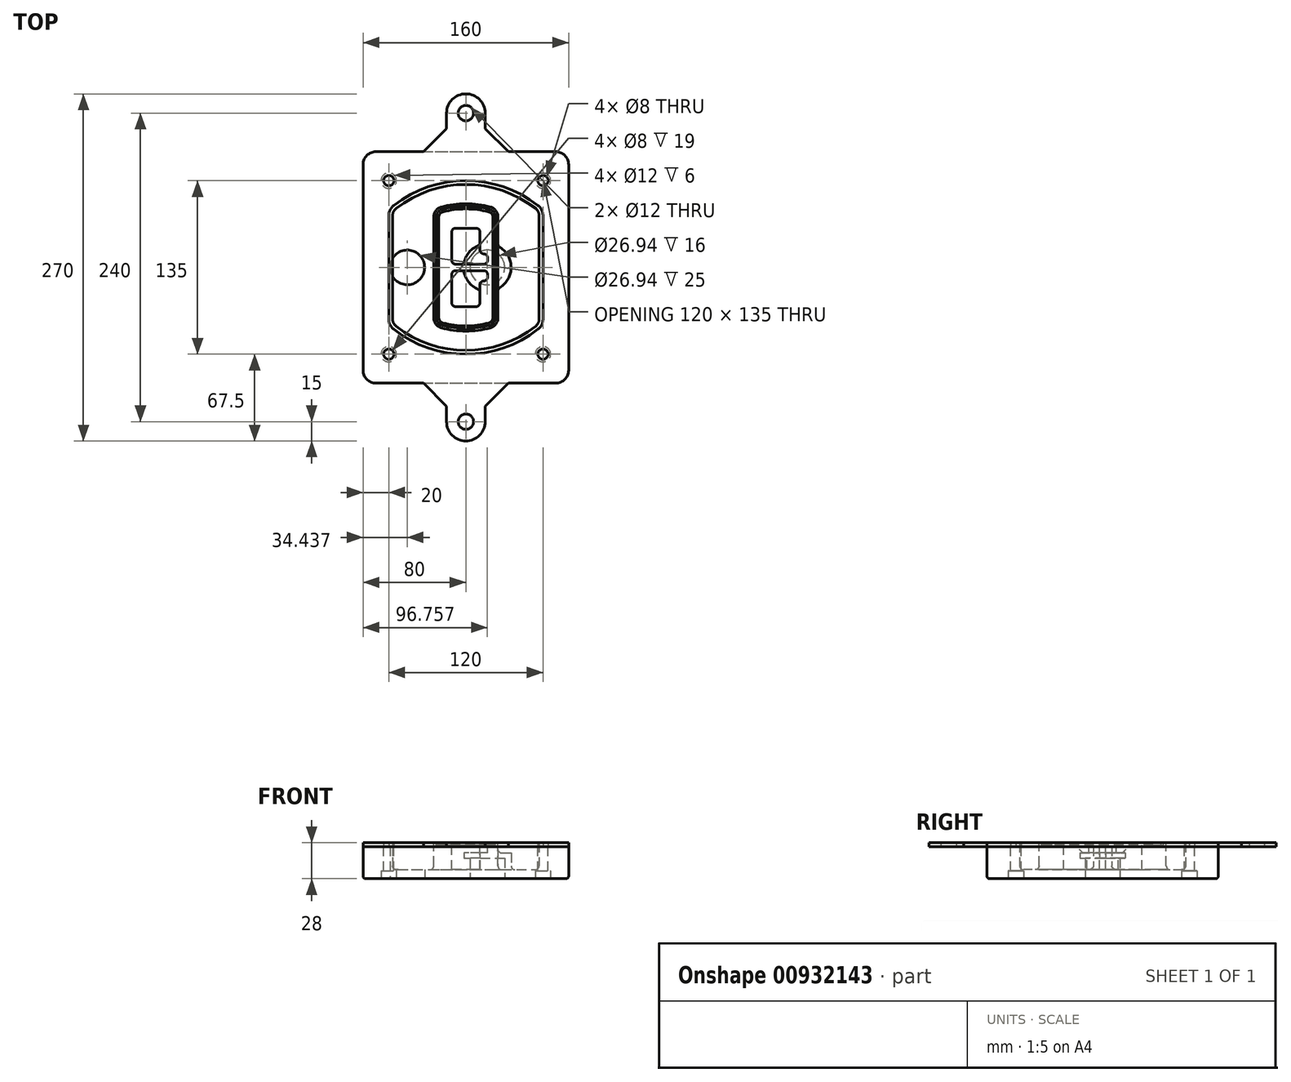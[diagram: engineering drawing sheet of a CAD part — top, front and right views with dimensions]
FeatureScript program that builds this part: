
annotation { "Feature Type Name" : "Feature", "Feature Type Description" : "" }
export const myFeature = defineFeature(function(context is Context, id is Id, definition is map)
    precondition{}
    {
        {
            var Q0;
            Q0=qCreatedBy(makeId("Top.planeOp"),FACE);
            var sketch = newSketch(context, id + "F0", { "sketchPlane" : qUnion([Q0])});
            skPoint(sketch, "E0.rect.middle", {"position": v(0, 0) * mm});
            skLineSegment(sketch, "E1.bottom", {"start": v(-70, -90) * mm, "end": v(70, -90) * mm});
            skLineSegment(sketch, "E1.top", {"start": v(-70, 90) * mm, "end": v(70, 90) * mm});
            skLineSegment(sketch, "E1.left", {"start": v(-80, -80) * mm, "end": v(-80, 80) * mm});
            skLineSegment(sketch, "E1.right", {"start": v(80, -80) * mm, "end": v(80, 80) * mm});
            skLineSegment(sketch, "E2", {"start": v(-80, 90) * mm, "end": v(80, -90) * mm, "construction": true});
            skLineSegment(sketch, "E3", {"start": v(80, 90) * mm, "end": v(-80, -90) * mm, "construction": true});
            skCircle(sketch, "E4", {"center": v(-60, 67.5) * mm, "radius": 4 * mm});
            skCircle(sketch, "E5", {"center": v(60, 67.5) * mm, "radius": 4 * mm});
            skCircle(sketch, "E6", {"center": v(60, -67.5) * mm, "radius": 4 * mm});
            skCircle(sketch, "E7", {"center": v(-60, -67.5) * mm, "radius": 4 * mm});
            skLineSegment(sketch, "E8", {"start": v(-60, 67.5) * mm, "end": v(60, 67.5) * mm, "construction": true});
            skLineSegment(sketch, "E9", {"start": v(60, 67.5) * mm, "end": v(60, -67.5) * mm, "construction": true});
            skLineSegment(sketch, "E10", {"start": v(60, -67.5) * mm, "end": v(-60, -67.5) * mm, "construction": true});
            skLineSegment(sketch, "E11", {"start": v(-60, -67.5) * mm, "end": v(-60, 67.5) * mm, "construction": true});
            skLineSegment(sketch, "E12", {"start": v(-60, 40.3) * mm, "end": v(-60, -40.3) * mm});
            skLineSegment(sketch, "E13", {"start": v(60, 40.3) * mm, "end": v(60, -40.3) * mm});
            skArc(sketch, "E14", {"start": v(56.15, 48.18) * mm, "mid": v(0, 67.5) * mm, "end": v(-56.15, 48.18) * mm});
            skArc(sketch, "E15", {"start": v(-56.15, -48.18) * mm, "mid": v(0, -67.5) * mm, "end": v(56.15, -48.18) * mm});
            skLineSegment(sketch, "E16", {"start": v(-60, 0) * mm, "end": v(60, 0) * mm, "construction": true});
            skPoint(sketch, "E17.visualSharp", {"position": v(-60, -45) * mm});
            skArc(sketch, "E17.filletArc", {"start": v(-60, -40.3) * mm, "mid": v(-58.99, -44.68) * mm, "end": v(-56.15, -48.18) * mm});
            skPoint(sketch, "E18.visualSharp", {"position": v(-60, 45) * mm});
            skArc(sketch, "E18.filletArc", {"start": v(-56.15, 48.18) * mm, "mid": v(-58.99, 44.68) * mm, "end": v(-60, 40.3) * mm});
            skPoint(sketch, "E19.visualSharp", {"position": v(60, 45) * mm});
            skArc(sketch, "E19.filletArc", {"start": v(60, 40.3) * mm, "mid": v(58.99, 44.68) * mm, "end": v(56.15, 48.18) * mm});
            skPoint(sketch, "E20.visualSharp", {"position": v(60, -45) * mm});
            skArc(sketch, "E20.filletArc", {"start": v(56.15, -48.18) * mm, "mid": v(58.99, -44.68) * mm, "end": v(60, -40.3) * mm});
            skPoint(sketch, "E21.visualSharp", {"position": v(-80, 90) * mm});
            skArc(sketch, "E21.filletArc", {"start": v(-70, 90) * mm, "mid": v(-77.07, 87.07) * mm, "end": v(-80, 80) * mm});
            skPoint(sketch, "E22.visualSharp", {"position": v(80, 90) * mm});
            skArc(sketch, "E22.filletArc", {"start": v(80, 80) * mm, "mid": v(77.07, 87.07) * mm, "end": v(70, 90) * mm});
            skPoint(sketch, "E23.visualSharp", {"position": v(80, -90) * mm});
            skArc(sketch, "E23.filletArc", {"start": v(70, -90) * mm, "mid": v(77.07, -87.07) * mm, "end": v(80, -80) * mm});
            skPoint(sketch, "E24.visualSharp", {"position": v(-80, -90) * mm});
            skArc(sketch, "E24.filletArc", {"start": v(-80, -80) * mm, "mid": v(-77.07, -87.07) * mm, "end": v(-70, -90) * mm});
            skArc(sketch, "E25.0", {"start": v(57, 40.3) * mm, "mid": v(56.3, 43.36) * mm, "end": v(54.3, 45.81) * mm});
            skLineSegment(sketch, "E25.1", {"start": v(57, 40.3) * mm, "end": v(57, -40.3) * mm});
            skArc(sketch, "E25.2", {"start": v(54.3, -45.81) * mm, "mid": v(56.3, -43.36) * mm, "end": v(57, -40.3) * mm});
            skArc(sketch, "E25.3", {"start": v(-54.3, -45.81) * mm, "mid": v(0, -64.5) * mm, "end": v(54.3, -45.81) * mm});
            skArc(sketch, "E25.4", {"start": v(-57, -40.3) * mm, "mid": v(-56.3, -43.36) * mm, "end": v(-54.3, -45.81) * mm});
            skArc(sketch, "E25.5", {"start": v(54.3, 45.81) * mm, "mid": v(0, 64.5) * mm, "end": v(-54.3, 45.81) * mm});
            skLineSegment(sketch, "E25.6", {"start": v(-57, 40.3) * mm, "end": v(-57, -40.3) * mm});
            skArc(sketch, "E25.7", {"start": v(-54.3, 45.81) * mm, "mid": v(-56.3, 43.36) * mm, "end": v(-57, 40.3) * mm});
            skArc(sketch, "E26.0", {"start": v(-58.62, 51.33) * mm, "mid": v(-62.58, 46.43) * mm, "end": v(-64, 40.3) * mm});
            skArc(sketch, "E26.1", {"start": v(58.62, 51.33) * mm, "mid": v(0, 71.5) * mm, "end": v(-58.62, 51.33) * mm});
            skArc(sketch, "E26.2", {"start": v(64, 40.3) * mm, "mid": v(62.58, 46.43) * mm, "end": v(58.62, 51.33) * mm});
            skLineSegment(sketch, "E26.3", {"start": v(64, 40.3) * mm, "end": v(64, -40.3) * mm});
            skArc(sketch, "E26.4", {"start": v(58.62, -51.33) * mm, "mid": v(62.58, -46.43) * mm, "end": v(64, -40.3) * mm});
            skLineSegment(sketch, "E26.5", {"start": v(-64, 40.3) * mm, "end": v(-64, -40.3) * mm});
            skArc(sketch, "E26.6", {"start": v(-58.62, -51.33) * mm, "mid": v(0, -71.5) * mm, "end": v(58.62, -51.33) * mm});
            skArc(sketch, "E26.7", {"start": v(-64, -40.3) * mm, "mid": v(-62.58, -46.43) * mm, "end": v(-58.62, -51.33) * mm});
            skSolve(sketch);
        }
        {
            var Q0;
            Q0=makeQuery(id+"F0.imprint","IMPRINT",FACE,{"disambiguationData":[TD([[makeQuery(id+"F0.imprint","IMPRINT",EDGE,{"derivedFrom":sQuery(id+"F0.wireOp",EDGE,"E1.bottom")}),1.0]])]});
            var Q1;
            Q1=makeQuery(id+"F0.imprint","IMPRINT",FACE,{"disambiguationData":[TD([[makeQuery(id+"F0.imprint","IMPRINT",EDGE,{"derivedFrom":sQuery(id+"F0.wireOp",EDGE,"E12")}),1.0]])]});
            var Q2;
            Q2=makeQuery(id+"F0.imprint","IMPRINT",FACE,{"disambiguationData":[TD([[makeQuery(id+"F0.imprint","IMPRINT",EDGE,{"derivedFrom":sQuery(id+"F0.wireOp",EDGE,"E25.0")}),1.0]])]});
            var Q3;
            Q3=makeQuery(id+"F0.imprint","IMPRINT",FACE,{"disambiguationData":[TD([[makeQuery(id+"F0.imprint","IMPRINT",EDGE,{"derivedFrom":sQuery(id+"F0.wireOp",EDGE,"E12")}),-1.0]])]});
            extrude(context, id + "F1", {"entities" : qUnion([Q0, Q1, Q2, Q3]), "oppositeDirection" : true, "depth" : 25 * mm});
        }
        {
            var Q0;
            Q0=makeQuery(id+"F0.imprint","IMPRINT",FACE,{"disambiguationData":[TD([[makeQuery(id+"F0.imprint","IMPRINT",EDGE,{"derivedFrom":sQuery(id+"F0.wireOp",EDGE,"E12")}),1.0]])]});
            extrude(context, id + "F2", {"entities" : qUnion([Q0]), "operationType" : NewBodyOperationType.ADD, "depth" : 3 * mm});
        }
        {
            var Q0;
            Q0=makeQuery(id+"F0.imprint","IMPRINT",FACE,{"disambiguationData":[TD([[makeQuery(id+"F0.imprint","IMPRINT",EDGE,{"derivedFrom":sQuery(id+"F0.wireOp",EDGE,"E25.0")}),1.0]])]});
            extrude(context, id + "F3", {"entities" : qUnion([Q0]), "operationType" : NewBodyOperationType.REMOVE, "oppositeDirection" : true, "depth" : 18 * mm});
        }
        {
            var Q0;
            Q0=makeQuery(id+"F2.opExtrude","CAP_FACE",FACE,{"disambiguationData":[OSD([sQuery(id+"F0.wireOp",EDGE,"E12"),sQuery(id+"F0.wireOp",EDGE,"E13"),sQuery(id+"F0.wireOp",EDGE,"E14"),sQuery(id+"F0.wireOp",EDGE,"E15"),sQuery(id+"F0.wireOp",EDGE,"E17.filletArc"),sQuery(id+"F0.wireOp",EDGE,"E18.filletArc"),sQuery(id+"F0.wireOp",EDGE,"E19.filletArc"),sQuery(id+"F0.wireOp",EDGE,"E20.filletArc"),sQuery(id+"F0.wireOp",EDGE,"E25.0"),sQuery(id+"F0.wireOp",EDGE,"E25.1"),sQuery(id+"F0.wireOp",EDGE,"E25.2"),sQuery(id+"F0.wireOp",EDGE,"E25.3"),sQuery(id+"F0.wireOp",EDGE,"E25.4"),sQuery(id+"F0.wireOp",EDGE,"E25.5"),sQuery(id+"F0.wireOp",EDGE,"E25.6"),sQuery(id+"F0.wireOp",EDGE,"E25.7")])],"isStart":false});
            var sketch = newSketch(context, id + "F4", { "sketchPlane" : qUnion([Q0])});
            skArc(sketch, "E27.0", {"start": v(-19.08, -46.97) * mm, "mid": v(0, -49.5) * mm, "end": v(19.08, -46.97) * mm});
            skArc(sketch, "E28.0", {"start": v(19.08, 46.97) * mm, "mid": v(0, 49.5) * mm, "end": v(-19.08, 46.97) * mm});
            skLineSegment(sketch, "E29", {"start": v(-25, 39.25) * mm, "end": v(-25, -39.25) * mm});
            skLineSegment(sketch, "E30", {"start": v(25, 39.25) * mm, "end": v(25, -39.25) * mm});
            skLineSegment(sketch, "E31", {"start": v(-25, 45.1) * mm, "end": v(25, 45.1) * mm, "construction": true});
            skLineSegment(sketch, "E32", {"start": v(-25, -45.1) * mm, "end": v(25, -45.1) * mm, "construction": true});
            skPoint(sketch, "E33.visualSharp", {"position": v(-25, 45.1) * mm});
            skArc(sketch, "E33.filletArc", {"start": v(-19.08, 46.97) * mm, "mid": v(-23.35, 44.11) * mm, "end": v(-25, 39.25) * mm});
            skPoint(sketch, "E34.visualSharp", {"position": v(25, 45.1) * mm});
            skArc(sketch, "E34.filletArc", {"start": v(25, 39.25) * mm, "mid": v(23.35, 44.11) * mm, "end": v(19.08, 46.97) * mm});
            skPoint(sketch, "E35.visualSharp", {"position": v(25, -45.1) * mm});
            skArc(sketch, "E35.filletArc", {"start": v(19.08, -46.97) * mm, "mid": v(23.35, -44.11) * mm, "end": v(25, -39.25) * mm});
            skPoint(sketch, "E36.visualSharp", {"position": v(-25, -45.1) * mm});
            skArc(sketch, "E36.filletArc", {"start": v(-25, -39.25) * mm, "mid": v(-23.35, -44.11) * mm, "end": v(-19.08, -46.97) * mm});
            skArc(sketch, "E37.0", {"start": v(54.3, 45.81) * mm, "mid": v(0, 64.5) * mm, "end": v(-54.3, 45.81) * mm});
            skArc(sketch, "E37.1", {"start": v(-54.3, 45.81) * mm, "mid": v(-56.3, 43.36) * mm, "end": v(-57, 40.3) * mm});
            skLineSegment(sketch, "E37.2", {"start": v(-57, 40.3) * mm, "end": v(-57, -40.3) * mm});
            skArc(sketch, "E37.3", {"start": v(-57, -40.3) * mm, "mid": v(-56.3, -43.36) * mm, "end": v(-54.3, -45.81) * mm});
            skArc(sketch, "E37.4", {"start": v(-54.3, -45.81) * mm, "mid": v(0, -64.5) * mm, "end": v(54.3, -45.81) * mm});
            skArc(sketch, "E37.5", {"start": v(54.3, -45.81) * mm, "mid": v(56.3, -43.36) * mm, "end": v(57, -40.3) * mm});
            skLineSegment(sketch, "E37.6", {"start": v(57, 40.3) * mm, "end": v(57, -40.3) * mm});
            skArc(sketch, "E37.7", {"start": v(57, 40.3) * mm, "mid": v(56.3, 43.36) * mm, "end": v(54.3, 45.81) * mm});
            skLineSegment(sketch, "E38.0", {"start": v(23, 39.25) * mm, "end": v(23, -39.25) * mm});
            skArc(sketch, "E38.1", {"start": v(18.56, -45.04) * mm, "mid": v(21.76, -42.9) * mm, "end": v(23, -39.25) * mm});
            skArc(sketch, "E38.2", {"start": v(-18.56, -45.04) * mm, "mid": v(0, -47.5) * mm, "end": v(18.56, -45.04) * mm});
            skArc(sketch, "E38.3", {"start": v(-23, -39.25) * mm, "mid": v(-21.76, -42.9) * mm, "end": v(-18.56, -45.04) * mm});
            skLineSegment(sketch, "E38.4", {"start": v(-23, 39.25) * mm, "end": v(-23, -39.25) * mm});
            skArc(sketch, "E38.5", {"start": v(23, 39.25) * mm, "mid": v(21.76, 42.9) * mm, "end": v(18.56, 45.04) * mm});
            skArc(sketch, "E38.6", {"start": v(-18.56, 45.04) * mm, "mid": v(-21.76, 42.9) * mm, "end": v(-23, 39.25) * mm});
            skArc(sketch, "E38.7", {"start": v(18.56, 45.04) * mm, "mid": v(0, 47.5) * mm, "end": v(-18.56, 45.04) * mm});
            skArc(sketch, "E39.0", {"start": v(21, 39.25) * mm, "mid": v(20.18, 41.68) * mm, "end": v(18.04, 43.1) * mm});
            skLineSegment(sketch, "E39.1", {"start": v(21, 39.25) * mm, "end": v(21, -39.25) * mm});
            skArc(sketch, "E39.2", {"start": v(18.04, -43.1) * mm, "mid": v(20.18, -41.68) * mm, "end": v(21, -39.25) * mm});
            skArc(sketch, "E39.3", {"start": v(-18.04, -43.1) * mm, "mid": v(0, -45.5) * mm, "end": v(18.04, -43.1) * mm});
            skArc(sketch, "E39.4", {"start": v(-21, -39.25) * mm, "mid": v(-20.18, -41.68) * mm, "end": v(-18.04, -43.1) * mm});
            skArc(sketch, "E39.5", {"start": v(18.04, 43.1) * mm, "mid": v(0, 45.5) * mm, "end": v(-18.04, 43.1) * mm});
            skLineSegment(sketch, "E39.6", {"start": v(-21, 39.25) * mm, "end": v(-21, -39.25) * mm});
            skArc(sketch, "E39.7", {"start": v(-18.04, 43.1) * mm, "mid": v(-20.18, 41.68) * mm, "end": v(-21, 39.25) * mm});
            skLineSegment(sketch, "E40", {"start": v(-25, 0) * mm, "end": v(25, 0) * mm, "construction": true});
            skLineSegment(sketch, "E41", {"start": v(-11, 5.5) * mm, "end": v(-11, 27.5) * mm});
            skLineSegment(sketch, "E42", {"start": v(-8, 30.5) * mm, "end": v(8, 30.5) * mm});
            skLineSegment(sketch, "E43", {"start": v(11, 27.5) * mm, "end": v(11, 13.5) * mm});
            skLineSegment(sketch, "E44", {"start": v(14, 10.5) * mm, "end": v(14, 10.5) * mm});
            skLineSegment(sketch, "E45", {"start": v(17, 7.5) * mm, "end": v(17, 5.5) * mm});
            skLineSegment(sketch, "E46", {"start": v(14, 2.5) * mm, "end": v(-8, 2.5) * mm});
            skPoint(sketch, "E47.visualSharp", {"position": v(-11, 30.5) * mm});
            skArc(sketch, "E47.filletArc", {"start": v(-8, 30.5) * mm, "mid": v(-10.12, 29.62) * mm, "end": v(-11, 27.5) * mm});
            skPoint(sketch, "E48.visualSharp", {"position": v(11, 30.5) * mm});
            skArc(sketch, "E48.filletArc", {"start": v(11, 27.5) * mm, "mid": v(10.12, 29.62) * mm, "end": v(8, 30.5) * mm});
            skPoint(sketch, "E49.visualSharp", {"position": v(11, 10.5) * mm});
            skArc(sketch, "E49.filletArc", {"start": v(11, 13.5) * mm, "mid": v(11.88, 11.38) * mm, "end": v(14, 10.5) * mm});
            skPoint(sketch, "E50.visualSharp", {"position": v(17, 10.5) * mm});
            skArc(sketch, "E50.filletArc", {"start": v(17, 7.5) * mm, "mid": v(16.12, 9.62) * mm, "end": v(14, 10.5) * mm});
            skPoint(sketch, "E51.visualSharp", {"position": v(17, 2.5) * mm});
            skArc(sketch, "E51.filletArc", {"start": v(14, 2.5) * mm, "mid": v(16.12, 3.38) * mm, "end": v(17, 5.5) * mm});
            skPoint(sketch, "E52.visualSharp", {"position": v(-11, 2.5) * mm});
            skArc(sketch, "E52.filletArc", {"start": v(-11, 5.5) * mm, "mid": v(-10.12, 3.38) * mm, "end": v(-8, 2.5) * mm});
            skLineSegment(sketch, "E53.0.MirrorCS", {"start": v(14, -2.5) * mm, "end": v(-8, -2.5) * mm});
            skArc(sketch, "E54.0.MirrorCS", {"start": v(-11, -5.5) * mm, "mid": v(-10.12, -3.38) * mm, "end": v(-8, -2.5) * mm});
            skLineSegment(sketch, "E55.0.MirrorCS", {"start": v(-11, -5.5) * mm, "end": v(-11, -27.5) * mm});
            skArc(sketch, "E56.0.MirrorCS", {"start": v(-8, -30.5) * mm, "mid": v(-10.12, -29.62) * mm, "end": v(-11, -27.5) * mm});
            skLineSegment(sketch, "E57.0.MirrorCS", {"start": v(-8, -30.5) * mm, "end": v(8, -30.5) * mm});
            skArc(sketch, "E58.0.MirrorCS", {"start": v(11, -27.5) * mm, "mid": v(10.12, -29.62) * mm, "end": v(8, -30.5) * mm});
            skLineSegment(sketch, "E59.0.MirrorCS", {"start": v(11, -27.5) * mm, "end": v(11, -13.5) * mm});
            skArc(sketch, "E60.0.MirrorCS", {"start": v(11, -13.5) * mm, "mid": v(11.88, -11.38) * mm, "end": v(14, -10.5) * mm});
            skArc(sketch, "E61.0.MirrorCS", {"start": v(17, -7.5) * mm, "mid": v(16.12, -9.62) * mm, "end": v(14, -10.5) * mm});
            skLineSegment(sketch, "E62.0.MirrorCS", {"start": v(17, -7.5) * mm, "end": v(17, -5.5) * mm});
            skArc(sketch, "E63.0.MirrorCS", {"start": v(14, -2.5) * mm, "mid": v(16.12, -3.38) * mm, "end": v(17, -5.5) * mm});
            skSolve(sketch);
        }
        {
            var Q0;
            Q0=makeQuery(id+"F4.imprint","IMPRINT",FACE,{"disambiguationData":[TD([[makeQuery(id+"F4.imprint","IMPRINT",EDGE,{"derivedFrom":sQuery(id+"F4.wireOp",EDGE,"E27.0")}),1.0]])]});
            var Q1;
            Q1=makeQuery(id+"F4.imprint","IMPRINT",FACE,{"disambiguationData":[TD([[makeQuery(id+"F4.imprint","IMPRINT",EDGE,{"derivedFrom":sQuery(id+"F4.wireOp",EDGE,"E38.0")}),-1.0]])]});
            var Q2;
            Q2=makeQuery(id+"F4.imprint","IMPRINT",FACE,{"disambiguationData":[TD([[makeQuery(id+"F4.imprint","IMPRINT",EDGE,{"derivedFrom":sQuery(id+"F4.wireOp",EDGE,"E39.0")}),1.0]])]});
            extrude(context, id + "F5", {"entities" : qUnion([Q0, Q1, Q2]), "operationType" : NewBodyOperationType.ADD, "endBound" : BoundingType.UP_TO_NEXT, "oppositeDirection" : true, "depth" : 25 * mm});
        }
        {
            var Q0;
            Q0=makeQuery(id+"F4.imprint","IMPRINT",FACE,{"disambiguationData":[TD([[makeQuery(id+"F4.imprint","IMPRINT",EDGE,{"derivedFrom":sQuery(id+"F4.wireOp",EDGE,"E38.0")}),-1.0]])]});
            extrude(context, id + "F6", {"entities" : qUnion([Q0]), "operationType" : NewBodyOperationType.REMOVE, "oppositeDirection" : true, "depth" : 2 * mm});
        }
        {
            var Q0;
            Q0=makeQuery(id+"F1.opExtrude","CAP_FACE",FACE,{"disambiguationData":[OSD([sQuery(id+"F0.wireOp",EDGE,"E1.bottom"),sQuery(id+"F0.wireOp",EDGE,"E1.top"),sQuery(id+"F0.wireOp",EDGE,"E1.left"),sQuery(id+"F0.wireOp",EDGE,"E1.right"),sQuery(id+"F0.wireOp",EDGE,"E4"),sQuery(id+"F0.wireOp",EDGE,"E5"),sQuery(id+"F0.wireOp",EDGE,"E6"),sQuery(id+"F0.wireOp",EDGE,"E7"),sQuery(id+"F0.wireOp",EDGE,"E21.filletArc"),sQuery(id+"F0.wireOp",EDGE,"E22.filletArc"),sQuery(id+"F0.wireOp",EDGE,"E23.filletArc"),sQuery(id+"F0.wireOp",EDGE,"E24.filletArc")])],"isStart":false});
            var sketch = newSketch(context, id + "F7", { "sketchPlane" : qUnion([Q0])});
            skCircle(sketch, "E64", {"center": v(16.76, 0) * mm, "radius": 13.47 * mm});
            skCircle(sketch, "E65", {"center": v(-45.56, 0) * mm, "radius": 13.47 * mm});
            skLineSegment(sketch, "E66", {"start": v(80, 0) * mm, "end": v(-80, 0) * mm});
            skCircle(sketch, "E67", {"center": v(16.76, 0) * mm, "radius": 18.47 * mm});
            skCircle(sketch, "E68", {"center": v(60, -67.5) * mm, "radius": 6 * mm});
            skCircle(sketch, "E69", {"center": v(-60, -67.5) * mm, "radius": 6 * mm});
            skCircle(sketch, "E70", {"center": v(-60, 67.5) * mm, "radius": 6 * mm});
            skCircle(sketch, "E71", {"center": v(60, 67.5) * mm, "radius": 6 * mm});
            skSolve(sketch);
        }
        {
            var Q0;
            {var subQ1=sQuery(id+"F7.wireOp",EDGE,"E66");var subQ4=sQuery(id+"F7.wireOp",EDGE,"E64");var subQ6=makeQuery(id+"F7.imprint","INTERSECT",VERTEX,{"disambiguationData":[OD(0.0)],"derivedFrom":[subQ4,subQ1]});Q0=makeQuery(id+"F7.imprint","IMPRINT",FACE,{"disambiguationData":[TD([[makeQuery(id+"F7.imprint","IMPRINT",EDGE,{"disambiguationData":[TD([[subQ6,-1.0]])],"derivedFrom":subQ4}),-1.0]])]});}
            var Q1;
            {var subQ0=sQuery(id+"F7.wireOp",EDGE,"E66");var subQ1=sQuery(id+"F7.wireOp",EDGE,"E64");var subQ3=makeQuery(id+"F7.imprint","INTERSECT",VERTEX,{"disambiguationData":[OD(0.0)],"derivedFrom":[subQ1,subQ0]});Q1=makeQuery(id+"F7.imprint","IMPRINT",FACE,{"disambiguationData":[TD([[makeQuery(id+"F7.imprint","IMPRINT",EDGE,{"disambiguationData":[TD([[subQ3,-1.0]])],"derivedFrom":subQ1}),1.0]])]});}
            var Q2;
            {var subQ0=sQuery(id+"F7.wireOp",EDGE,"E66");var subQ1=sQuery(id+"F7.wireOp",EDGE,"E64");var subQ3=makeQuery(id+"F7.imprint","INTERSECT",VERTEX,{"disambiguationData":[OD(0.0)],"derivedFrom":[subQ1,subQ0]});Q2=makeQuery(id+"F7.imprint","IMPRINT",FACE,{"disambiguationData":[TD([[makeQuery(id+"F7.imprint","IMPRINT",EDGE,{"disambiguationData":[TD([[subQ3,1.0]])],"derivedFrom":subQ1}),1.0]])]});}
            var Q3;
            {var subQ1=sQuery(id+"F7.wireOp",EDGE,"E66");var subQ4=sQuery(id+"F7.wireOp",EDGE,"E64");var subQ6=makeQuery(id+"F7.imprint","INTERSECT",VERTEX,{"disambiguationData":[OD(0.0)],"derivedFrom":[subQ4,subQ1]});Q3=makeQuery(id+"F7.imprint","IMPRINT",FACE,{"disambiguationData":[TD([[makeQuery(id+"F7.imprint","IMPRINT",EDGE,{"disambiguationData":[TD([[subQ6,1.0]])],"derivedFrom":subQ4}),-1.0]])]});}
            extrude(context, id + "F8", {"entities" : qUnion([Q0, Q1, Q2, Q3]), "operationType" : NewBodyOperationType.ADD, "oppositeDirection" : true, "depth" : 20 * mm});
        }
        {
            var Q0;
            {var subQ0=sQuery(id+"F7.wireOp",EDGE,"E66");var subQ1=sQuery(id+"F7.wireOp",EDGE,"E64");var subQ3=makeQuery(id+"F7.imprint","INTERSECT",VERTEX,{"disambiguationData":[OD(0.0)],"derivedFrom":[subQ1,subQ0]});Q0=makeQuery(id+"F7.imprint","IMPRINT",FACE,{"disambiguationData":[TD([[makeQuery(id+"F7.imprint","IMPRINT",EDGE,{"disambiguationData":[TD([[subQ3,-1.0]])],"derivedFrom":subQ1}),1.0]])]});}
            var Q1;
            {var subQ0=sQuery(id+"F7.wireOp",EDGE,"E66");var subQ1=sQuery(id+"F7.wireOp",EDGE,"E64");var subQ3=makeQuery(id+"F7.imprint","INTERSECT",VERTEX,{"disambiguationData":[OD(0.0)],"derivedFrom":[subQ1,subQ0]});Q1=makeQuery(id+"F7.imprint","IMPRINT",FACE,{"disambiguationData":[TD([[makeQuery(id+"F7.imprint","IMPRINT",EDGE,{"disambiguationData":[TD([[subQ3,1.0]])],"derivedFrom":subQ1}),1.0]])]});}
            extrude(context, id + "F9", {"entities" : qUnion([Q0, Q1]), "operationType" : NewBodyOperationType.REMOVE, "oppositeDirection" : true, "depth" : 16 * mm});
        }
        {
            var Q0;
            {var subQ0=sQuery(id+"F7.wireOp",EDGE,"E66");var subQ1=sQuery(id+"F7.wireOp",EDGE,"E65");var subQ3=makeQuery(id+"F7.imprint","INTERSECT",VERTEX,{"disambiguationData":[OD(0.0)],"derivedFrom":[subQ1,subQ0]});Q0=makeQuery(id+"F7.imprint","IMPRINT",FACE,{"disambiguationData":[TD([[makeQuery(id+"F7.imprint","IMPRINT",EDGE,{"disambiguationData":[TD([[subQ3,-1.0]])],"derivedFrom":subQ1}),1.0]])]});}
            var Q1;
            {var subQ0=sQuery(id+"F7.wireOp",EDGE,"E66");var subQ1=sQuery(id+"F7.wireOp",EDGE,"E65");var subQ3=makeQuery(id+"F7.imprint","INTERSECT",VERTEX,{"disambiguationData":[OD(0.0)],"derivedFrom":[subQ1,subQ0]});Q1=makeQuery(id+"F7.imprint","IMPRINT",FACE,{"disambiguationData":[TD([[makeQuery(id+"F7.imprint","IMPRINT",EDGE,{"disambiguationData":[TD([[subQ3,1.0]])],"derivedFrom":subQ1}),1.0]])]});}
            extrude(context, id + "F10", {"entities" : qUnion([Q0, Q1]), "operationType" : NewBodyOperationType.REMOVE, "oppositeDirection" : true, "depth" : 25 * mm});
        }
        {
            var Q0;
            Q0=makeQuery(id+"F7.imprint","IMPRINT",FACE,{"disambiguationData":[TD([[makeQuery(id+"F7.imprint","IMPRINT",EDGE,{"derivedFrom":sQuery(id+"F7.wireOp",EDGE,"E68")}),1.0]])]});
            var Q1;
            Q1=makeQuery(id+"F7.imprint","IMPRINT",FACE,{"disambiguationData":[TD([[makeQuery(id+"F7.imprint","IMPRINT",EDGE,{"derivedFrom":makeQuery(id+"F1.opExtrude","CAP_EDGE",EDGE,{"disambiguationData":[OSD([sQuery(id+"F0.wireOp",EDGE,"E5")])],"isStart":false})}),-1.0]])]});
            var Q2;
            Q2=makeQuery(id+"F7.imprint","IMPRINT",FACE,{"disambiguationData":[TD([[makeQuery(id+"F7.imprint","IMPRINT",EDGE,{"derivedFrom":sQuery(id+"F7.wireOp",EDGE,"E69")}),1.0]])]});
            var Q3;
            Q3=makeQuery(id+"F7.imprint","IMPRINT",FACE,{"disambiguationData":[TD([[makeQuery(id+"F7.imprint","IMPRINT",EDGE,{"derivedFrom":makeQuery(id+"F1.opExtrude","CAP_EDGE",EDGE,{"disambiguationData":[OSD([sQuery(id+"F0.wireOp",EDGE,"E4")])],"isStart":false})}),-1.0]])]});
            var Q4;
            Q4=makeQuery(id+"F7.imprint","IMPRINT",FACE,{"disambiguationData":[TD([[makeQuery(id+"F7.imprint","IMPRINT",EDGE,{"derivedFrom":sQuery(id+"F7.wireOp",EDGE,"E70")}),1.0]])]});
            var Q5;
            Q5=makeQuery(id+"F7.imprint","IMPRINT",FACE,{"disambiguationData":[TD([[makeQuery(id+"F7.imprint","IMPRINT",EDGE,{"derivedFrom":makeQuery(id+"F1.opExtrude","CAP_EDGE",EDGE,{"disambiguationData":[OSD([sQuery(id+"F0.wireOp",EDGE,"E7")])],"isStart":false})}),-1.0]])]});
            var Q6;
            Q6=makeQuery(id+"F7.imprint","IMPRINT",FACE,{"disambiguationData":[TD([[makeQuery(id+"F7.imprint","IMPRINT",EDGE,{"derivedFrom":sQuery(id+"F7.wireOp",EDGE,"E71")}),1.0]])]});
            var Q7;
            Q7=makeQuery(id+"F7.imprint","IMPRINT",FACE,{"disambiguationData":[TD([[makeQuery(id+"F7.imprint","IMPRINT",EDGE,{"derivedFrom":makeQuery(id+"F1.opExtrude","CAP_EDGE",EDGE,{"disambiguationData":[OSD([sQuery(id+"F0.wireOp",EDGE,"E6")])],"isStart":false})}),-1.0]])]});
            extrude(context, id + "F11", {"entities" : qUnion([Q0, Q1, Q2, Q3, Q4, Q5, Q6, Q7]), "operationType" : NewBodyOperationType.REMOVE, "oppositeDirection" : true, "depth" : 6 * mm});
        }
        {
            var Q0;
            Q0=makeQuery(id+"F9.boolean.opBoolean","COPY",FACE,{"derivedFrom":makeQuery(id+"F9.opExtrude","CAP_FACE",FACE,{"disambiguationData":[OSD([sQuery(id+"F7.wireOp",EDGE,"E64")])],"isStart":false})});
            var sketch = newSketch(context, id + "F12", { "sketchPlane" : qUnion([Q0])});
            skArc(sketch, "E72.0", {"start": v(11, 17.55) * mm, "mid": v(2.57, 11.82) * mm, "end": v(-1.54, 2.5) * mm});
            skArc(sketch, "E72.1", {"start": v(-1.54, -2.5) * mm, "mid": v(2.57, -11.82) * mm, "end": v(11, -17.55) * mm});
            skLineSegment(sketch, "E73", {"start": v(-1.54, -2.5) * mm, "end": v(14, -2.5) * mm});
            skLineSegment(sketch, "E74.0", {"start": v(14, 2.5) * mm, "end": v(-1.54, 2.5) * mm});
            skArc(sketch, "E74.1", {"start": v(14, 2.5) * mm, "mid": v(16.12, 3.38) * mm, "end": v(17, 5.5) * mm});
            skLineSegment(sketch, "E74.2", {"start": v(17, 7.5) * mm, "end": v(17, 5.5) * mm});
            skArc(sketch, "E74.3", {"start": v(17, 7.5) * mm, "mid": v(16.12, 9.62) * mm, "end": v(14, 10.5) * mm});
            skArc(sketch, "E74.4", {"start": v(11, 13.5) * mm, "mid": v(11.88, 11.38) * mm, "end": v(14, 10.5) * mm});
            skLineSegment(sketch, "E74.5", {"start": v(11, 17.55) * mm, "end": v(11, 13.5) * mm});
            skLineSegment(sketch, "E74.7", {"start": v(14, -2.5) * mm, "end": v(-1.54, -2.5) * mm});
            skArc(sketch, "E74.8", {"start": v(14, -2.5) * mm, "mid": v(16.12, -3.38) * mm, "end": v(17, -5.5) * mm});
            skLineSegment(sketch, "E74.9", {"start": v(17, -7.5) * mm, "end": v(17, -5.5) * mm});
            skArc(sketch, "E74.10", {"start": v(17, -7.5) * mm, "mid": v(16.12, -9.62) * mm, "end": v(14, -10.5) * mm});
            skArc(sketch, "E74.11", {"start": v(11, -13.5) * mm, "mid": v(11.88, -11.38) * mm, "end": v(14, -10.5) * mm});
            skLineSegment(sketch, "E74.12", {"start": v(11, -17.55) * mm, "end": v(11, -13.5) * mm});
            skPoint(sketch, "E75.orphan", {"position": v(11, -27.5) * mm});
            skPoint(sketch, "E76.orphan", {"position": v(-8, -2.5) * mm});
            skPoint(sketch, "E77.orphan", {"position": v(-8, 2.5) * mm});
            skPoint(sketch, "E78.orphan", {"position": v(11, 27.5) * mm});
            skSolve(sketch);
        }
        {
            var Q0;
            {var subQ7=sQuery(id+"F12.wireOp",EDGE,"E72.0");var subQ14=sQuery(id+"F12.wireOp",EDGE,"E72.1");var subQ16=sQuery(id+"F12.wireOp",EDGE,"E74.1");var subQ18=sQuery(id+"F12.wireOp",EDGE,"E74.8");Q0=qUnion([makeQuery(id+"F12.imprint","IMPRINT",FACE,{"disambiguationData":[TD([[makeQuery(id+"F12.imprint","IMPRINT",EDGE,{"derivedFrom":subQ7}),1.0]])]}),makeQuery(id+"F12.imprint","IMPRINT",FACE,{"disambiguationData":[TD([[makeQuery(id+"F12.imprint","IMPRINT",EDGE,{"derivedFrom":subQ14}),1.0]])]}),makeQuery(id+"F12.imprint","IMPRINT",FACE,{"disambiguationData":[TD([[makeQuery(id+"F12.imprint","IMPRINT",EDGE,{"derivedFrom":subQ16}),1.0]])]}),makeQuery(id+"F12.imprint","IMPRINT",FACE,{"disambiguationData":[TD([[makeQuery(id+"F12.imprint","IMPRINT",EDGE,{"derivedFrom":subQ18}),-1.0]])]})]);}
            var Q1;
            Q1=makeQuery(id+"F5.boolean.opBoolean","SPLIT",FACE,{"disambiguationData":[TD([makeQuery(id+"F5.opExtrude","SWEPT_FACE",FACE,{"disambiguationData":[OSD([sQuery(id+"F4.wireOp",EDGE,"E41")])]})])],"derivedFrom":makeQuery(id+"F3.boolean.opBoolean","COPY",FACE,{"derivedFrom":makeQuery(id+"F3.opExtrude","CAP_FACE",FACE,{"disambiguationData":[OSD([sQuery(id+"F0.wireOp",EDGE,"E25.0"),sQuery(id+"F0.wireOp",EDGE,"E25.1"),sQuery(id+"F0.wireOp",EDGE,"E25.2"),sQuery(id+"F0.wireOp",EDGE,"E25.3"),sQuery(id+"F0.wireOp",EDGE,"E25.4"),sQuery(id+"F0.wireOp",EDGE,"E25.5"),sQuery(id+"F0.wireOp",EDGE,"E25.6"),sQuery(id+"F0.wireOp",EDGE,"E25.7")])],"isStart":false})})});
            extrude(context, id + "F13", {"entities" : qUnion([Q0]), "operationType" : NewBodyOperationType.REMOVE, "endBound" : BoundingType.UP_TO_SURFACE, "endBoundEntityFace" : qUnion([Q1]), "depth" : 25 * mm});
        }
        {
            var Q0;
            Q0=makeQuery(id+"F3.boolean.opBoolean","COPY",EDGE,{"derivedFrom":makeQuery(id+"F3.opExtrude","CAP_EDGE",EDGE,{"disambiguationData":[OSD([sQuery(id+"F0.wireOp",EDGE,"E25.6")])],"isStart":false})});
            var Q1;
            Q1=makeQuery(id+"F8.boolean.opBoolean","INTERSECT",EDGE,{"derivedFrom":[makeQuery(id+"F5.opExtrude","SWEPT_FACE",FACE,{"disambiguationData":[OSD([sQuery(id+"F4.wireOp",EDGE,"E30")])]}),makeQuery(id+"F8.opExtrude","CAP_FACE",FACE,{"disambiguationData":[OSD([sQuery(id+"F7.wireOp",EDGE,"E67")])],"isStart":false})]});
            var Q2;
            Q2=makeQuery(id+"F8.boolean.opBoolean","INTERSECT",EDGE,{"disambiguationData":[OD(1.0)],"derivedFrom":[makeQuery(id+"F5.opExtrude","SWEPT_FACE",FACE,{"disambiguationData":[OSD([sQuery(id+"F4.wireOp",EDGE,"E30")])]}),makeQuery(id+"F8.opExtrude","SWEPT_FACE",FACE,{"disambiguationData":[OSD([sQuery(id+"F7.wireOp",EDGE,"E67")])]})]});
            var Q3;
            {var subQ0=sQuery(id+"F4.wireOp",EDGE,"E30");Q3=makeQuery(id+"F8.boolean.opBoolean","SPLIT",EDGE,{"disambiguationData":[TD([makeQuery(id+"F5.opExtrude","SWEPT_FACE",FACE,{"disambiguationData":[OSD([sQuery(id+"F4.wireOp",EDGE,"E35.filletArc")])]})])],"derivedFrom":makeQuery(id+"F5.opExtrude","CAP_EDGE",EDGE,{"disambiguationData":[OSD([subQ0])],"isStart":false})});}
            var Q4;
            {var subQ0=sQuery(id+"F0.wireOp",EDGE,"E25.7");var subQ1=sQuery(id+"F0.wireOp",EDGE,"E25.1");var subQ2=sQuery(id+"F0.wireOp",EDGE,"E25.6");var subQ3=sQuery(id+"F0.wireOp",EDGE,"E25.5");var subQ4=sQuery(id+"F0.wireOp",EDGE,"E25.4");var subQ5=sQuery(id+"F0.wireOp",EDGE,"E25.0");var subQ6=sQuery(id+"F0.wireOp",EDGE,"E25.2");var subQ7=sQuery(id+"F0.wireOp",EDGE,"E25.3");Q4=makeQuery(id+"F8.boolean.opBoolean","INTERSECT",EDGE,{"derivedFrom":[makeQuery(id+"F5.boolean.opBoolean","SPLIT",FACE,{"disambiguationData":[TD([makeQuery(id+"F2.opExtrude","SWEPT_FACE",FACE,{"disambiguationData":[OSD([subQ5])]})])],"derivedFrom":makeQuery(id+"F3.boolean.opBoolean","COPY",FACE,{"derivedFrom":makeQuery(id+"F3.opExtrude","CAP_FACE",FACE,{"disambiguationData":[OSD([subQ5,subQ1,subQ6,subQ7,subQ4,subQ3,subQ2,subQ0])],"isStart":false})})}),makeQuery(id+"F8.opExtrude","SWEPT_FACE",FACE,{"disambiguationData":[OSD([sQuery(id+"F7.wireOp",EDGE,"E67")])]})]});}
            var Q5;
            Q5=makeQuery(id+"F8.boolean.opBoolean","INTERSECT",EDGE,{"disambiguationData":[OD(0.0)],"derivedFrom":[makeQuery(id+"F5.opExtrude","SWEPT_FACE",FACE,{"disambiguationData":[OSD([sQuery(id+"F4.wireOp",EDGE,"E30")])]}),makeQuery(id+"F8.opExtrude","SWEPT_FACE",FACE,{"disambiguationData":[OSD([sQuery(id+"F7.wireOp",EDGE,"E67")])]})]});
            fillet(context, id + "F14", {"entities" : qUnion([Q0, Q1, Q2, Q3, Q4, Q5]), "radius" : 3 * mm, "tangentPropagation" : true, "allowEdgeOverflow" : false});
        }
        {
            var Q0;
            Q0=makeQuery(id+"F1.opExtrude","CAP_EDGE",EDGE,{"disambiguationData":[OSD([sQuery(id+"F0.wireOp",EDGE,"E1.bottom")])],"isStart":false});
            fillet(context, id + "F15", {"entities" : qUnion([Q0]), "radius" : 2 * mm, "tangentPropagation" : true, "allowEdgeOverflow" : false});
        }
        {
            var Q0;
            {var subQ0=sQuery(id+"F0.wireOp",EDGE,"E21.filletArc");var subQ1=sQuery(id+"F0.wireOp",EDGE,"E7");var subQ2=sQuery(id+"F0.wireOp",EDGE,"E6");var subQ3=sQuery(id+"F0.wireOp",EDGE,"E5");var subQ4=sQuery(id+"F0.wireOp",EDGE,"E4");var subQ5=sQuery(id+"F0.wireOp",EDGE,"E22.filletArc");var subQ6=sQuery(id+"F0.wireOp",EDGE,"E1.bottom");var subQ7=sQuery(id+"F0.wireOp",EDGE,"E1.right");var subQ8=sQuery(id+"F0.wireOp",EDGE,"E1.top");var subQ9=sQuery(id+"F0.wireOp",EDGE,"E1.left");var subQ10=sQuery(id+"F0.wireOp",EDGE,"E23.filletArc");var subQ11=sQuery(id+"F0.wireOp",EDGE,"E24.filletArc");Q0=makeQuery(id+"F2.boolean.opBoolean","SPLIT",FACE,{"disambiguationData":[TD([makeQuery(id+"F1.opExtrude","SWEPT_FACE",FACE,{"disambiguationData":[OSD([subQ6])]})])],"derivedFrom":makeQuery(id+"F1.opExtrude","CAP_FACE",FACE,{"disambiguationData":[OSD([subQ6,subQ8,subQ9,subQ7,subQ4,subQ3,subQ2,subQ1,subQ0,subQ5,subQ10,subQ11])],"isStart":true})});}
            var sketch = newSketch(context, id + "F16", { "sketchPlane" : qUnion([Q0])});
            skLineSegment(sketch, "E79", {"start": v(-33, 90) * mm, "end": v(-15, 108) * mm});
            skLineSegment(sketch, "E80", {"start": v(-15, 108) * mm, "end": v(-15, 120) * mm});
            skLineSegment(sketch, "E81", {"start": v(33, 90) * mm, "end": v(15, 108) * mm});
            skLineSegment(sketch, "E82", {"start": v(15, 108) * mm, "end": v(15, 120) * mm});
            skCircle(sketch, "E83", {"center": v(0, 120) * mm, "radius": 6 * mm});
            skPoint(sketch, "E83.centerSnap0", {"position": v(0, 90) * mm});
            skArc(sketch, "E84", {"start": v(15, 120) * mm, "mid": v(0, 135) * mm, "end": v(-15, 120) * mm});
            skLineSegment(sketch, "E85", {"start": v(-80, 0) * mm, "end": v(80, 0) * mm, "construction": true});
            skArc(sketch, "E86.MirrorCS", {"start": v(15, -120) * mm, "mid": v(0, -135) * mm, "end": v(-15, -120) * mm});
            skLineSegment(sketch, "E87.MirrorCS", {"start": v(33, -90) * mm, "end": v(15, -108) * mm});
            skPoint(sketch, "E88.MirrorP", {"position": v(0, -90) * mm});
            skLineSegment(sketch, "E89.MirrorCS", {"start": v(-15, -108) * mm, "end": v(-15, -120) * mm});
            skLineSegment(sketch, "E90.MirrorCS", {"start": v(15, -108) * mm, "end": v(15, -120) * mm});
            skLineSegment(sketch, "E91.MirrorCS", {"start": v(-33, -90) * mm, "end": v(-15, -108) * mm});
            skCircle(sketch, "E92.MirrorC", {"center": v(0, -120) * mm, "radius": 6 * mm});
            skSolve(sketch);
        }
        {
            var Q0;
            Q0=makeQuery(id+"F16.imprint","IMPRINT",FACE,{"disambiguationData":[TD([[makeQuery(id+"F16.imprint","IMPRINT",EDGE,{"derivedFrom":makeQuery(id+"F1.opExtrude","CAP_EDGE",EDGE,{"disambiguationData":[OSD([sQuery(id+"F0.wireOp",EDGE,"E1.left")])],"isStart":true})}),-1.0]])]});
            var Q1;
            {var subQ1=sQuery(id+"F16.wireOp",EDGE,"E87.MirrorCS");Q1=makeQuery(id+"F16.imprint","IMPRINT",FACE,{"disambiguationData":[TD([[makeQuery(id+"F16.imprint","IMPRINT",EDGE,{"derivedFrom":subQ1}),-1.0]])]});}
            var Q2;
            {var subQ1=sQuery(id+"F16.wireOp",EDGE,"E79");Q2=makeQuery(id+"F16.imprint","IMPRINT",FACE,{"disambiguationData":[TD([[makeQuery(id+"F16.imprint","IMPRINT",EDGE,{"derivedFrom":subQ1}),-1.0]])]});}
            var Q3;
            Q3=makeQuery(id+"F2.opExtrude","CAP_FACE",FACE,{"disambiguationData":[OSD([sQuery(id+"F0.wireOp",EDGE,"E12"),sQuery(id+"F0.wireOp",EDGE,"E13"),sQuery(id+"F0.wireOp",EDGE,"E14"),sQuery(id+"F0.wireOp",EDGE,"E15"),sQuery(id+"F0.wireOp",EDGE,"E17.filletArc"),sQuery(id+"F0.wireOp",EDGE,"E18.filletArc"),sQuery(id+"F0.wireOp",EDGE,"E19.filletArc"),sQuery(id+"F0.wireOp",EDGE,"E20.filletArc"),sQuery(id+"F0.wireOp",EDGE,"E25.0"),sQuery(id+"F0.wireOp",EDGE,"E25.1"),sQuery(id+"F0.wireOp",EDGE,"E25.2"),sQuery(id+"F0.wireOp",EDGE,"E25.3"),sQuery(id+"F0.wireOp",EDGE,"E25.4"),sQuery(id+"F0.wireOp",EDGE,"E25.5"),sQuery(id+"F0.wireOp",EDGE,"E25.6"),sQuery(id+"F0.wireOp",EDGE,"E25.7")])],"isStart":false});
            extrude(context, id + "F17", {"entities" : qUnion([Q0, Q1, Q2]), "endBound" : BoundingType.UP_TO_SURFACE, "depth" : 25 * mm, "endBoundEntityFace" : qUnion([Q3]), "offsetDistance" : 25 * mm});
        }
    });
